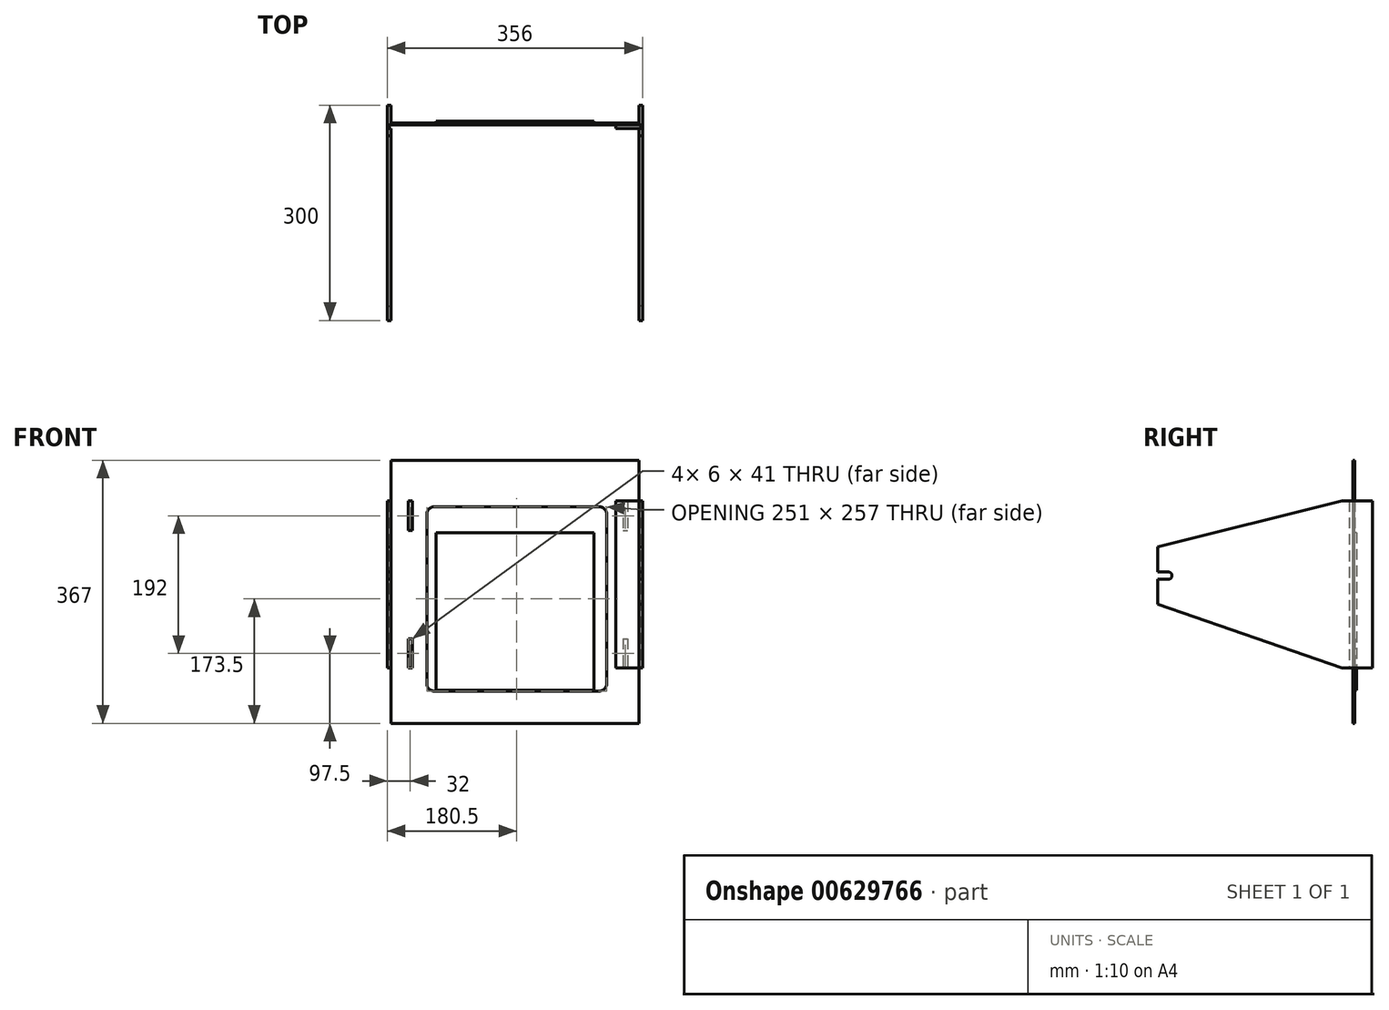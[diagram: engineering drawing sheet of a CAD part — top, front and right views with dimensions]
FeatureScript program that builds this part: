
annotation { "Feature Type Name" : "Feature", "Feature Type Description" : "" }
export const myFeature = defineFeature(function(context is Context, id is Id, definition is map)
    precondition{}
    {
        {
            var Q0;
            Q0=qCreatedBy(makeId("Front.planeOp"),FACE);
            var sketch = newSketch(context, id + "F0", { "sketchPlane" : qUnion([Q0])});
            skLineSegment(sketch, "E0.bottom", {"start": v(118, -138.5) * mm, "end": v(-113, -138.5) * mm});
            skLineSegment(sketch, "E0.top", {"start": v(118, 118.5) * mm, "end": v(-113, 118.5) * mm});
            skLineSegment(sketch, "E0.left", {"start": v(128, -128.5) * mm, "end": v(128, 108.5) * mm});
            skLineSegment(sketch, "E0.right", {"start": v(-123, -128.5) * mm, "end": v(-123, 108.5) * mm});
            skLineSegment(sketch, "E1.bottom", {"start": v(173, -183.5) * mm, "end": v(-173, -183.5) * mm});
            skLineSegment(sketch, "E1.top", {"start": v(173, 183.5) * mm, "end": v(-173, 183.5) * mm});
            skLineSegment(sketch, "E1.left", {"start": v(173, -183.5) * mm, "end": v(173, 183.5) * mm});
            skLineSegment(sketch, "E1.right", {"start": v(-173, -183.5) * mm, "end": v(-173, 183.5) * mm});
            skPoint(sketch, "E1.middle", {"position": v(0, 0) * mm});
            skLineSegment(sketch, "E2.bottom", {"start": v(-110, 82.5) * mm, "end": v(110, 82.5) * mm});
            skLineSegment(sketch, "E2.top", {"start": v(-110, -137.5) * mm, "end": v(110, -137.5) * mm});
            skLineSegment(sketch, "E2.left", {"start": v(-110, 82.5) * mm, "end": v(-110, -137.5) * mm});
            skLineSegment(sketch, "E2.right", {"start": v(110, 82.5) * mm, "end": v(110, -137.5) * mm});
            skLineSegment(sketch, "E3", {"start": v(0, 82.5) * mm, "end": v(0, 183.5) * mm, "construction": true});
            skLineSegment(sketch, "E4.bottom", {"start": v(-149, 126.5) * mm, "end": v(-143, 126.5) * mm});
            skLineSegment(sketch, "E4.top", {"start": v(-149, 85.5) * mm, "end": v(-143, 85.5) * mm});
            skLineSegment(sketch, "E4.left", {"start": v(-149, 126.5) * mm, "end": v(-149, 85.5) * mm});
            skLineSegment(sketch, "E4.right", {"start": v(-143, 126.5) * mm, "end": v(-143, 85.5) * mm});
            skLineSegment(sketch, "E5.bottom", {"start": v(-149, -65.5) * mm, "end": v(-143, -65.5) * mm});
            skLineSegment(sketch, "E5.top", {"start": v(-149, -106.5) * mm, "end": v(-143, -106.5) * mm});
            skLineSegment(sketch, "E5.left", {"start": v(-149, -65.5) * mm, "end": v(-149, -106.5) * mm});
            skLineSegment(sketch, "E5.right", {"start": v(-143, -65.5) * mm, "end": v(-143, -106.5) * mm});
            skLineSegment(sketch, "E6.bottom", {"start": v(151, 126.5) * mm, "end": v(157, 126.5) * mm});
            skLineSegment(sketch, "E6.top", {"start": v(151, 85.5) * mm, "end": v(157, 85.5) * mm});
            skLineSegment(sketch, "E6.left", {"start": v(151, 126.5) * mm, "end": v(151, 85.5) * mm});
            skLineSegment(sketch, "E6.right", {"start": v(157, 126.5) * mm, "end": v(157, 85.5) * mm});
            skLineSegment(sketch, "E7.bottom", {"start": v(151, -65.5) * mm, "end": v(157, -65.5) * mm});
            skLineSegment(sketch, "E7.top", {"start": v(151, -106.5) * mm, "end": v(157, -106.5) * mm});
            skLineSegment(sketch, "E7.left", {"start": v(151, -65.5) * mm, "end": v(151, -106.5) * mm});
            skLineSegment(sketch, "E7.right", {"start": v(157, -65.5) * mm, "end": v(157, -106.5) * mm});
            skPoint(sketch, "E8.visualSharp", {"position": v(-123, 118.5) * mm});
            skArc(sketch, "E8.filletArc", {"start": v(-113, 118.5) * mm, "mid": v(-120.07, 115.57) * mm, "end": v(-123, 108.5) * mm});
            skPoint(sketch, "E9.visualSharp", {"position": v(128, 118.5) * mm});
            skArc(sketch, "E9.filletArc", {"start": v(128, 108.5) * mm, "mid": v(125.07, 115.57) * mm, "end": v(118, 118.5) * mm});
            skPoint(sketch, "E10.visualSharp", {"position": v(128, -138.5) * mm});
            skArc(sketch, "E10.filletArc", {"start": v(118, -138.5) * mm, "mid": v(125.07, -135.57) * mm, "end": v(128, -128.5) * mm});
            skPoint(sketch, "E11.visualSharp", {"position": v(-123, -138.5) * mm});
            skArc(sketch, "E11.filletArc", {"start": v(-123, -128.5) * mm, "mid": v(-120.07, -135.57) * mm, "end": v(-113, -138.5) * mm});
            skLineSegment(sketch, "E12", {"start": v(110, 82.5) * mm, "end": v(-110, -137.5) * mm, "construction": true});
            skLineSegment(sketch, "E13", {"start": v(-110, 82.5) * mm, "end": v(110, -137.5) * mm, "construction": true});
            skSolve(sketch);
        }
        {
            var Q0;
            Q0=makeQuery(id+"F0.imprint","IMPRINT",FACE,{"disambiguationData":[TD([[makeQuery(id+"F0.imprint","IMPRINT",EDGE,{"derivedFrom":sQuery(id+"F0.wireOp",EDGE,"E0.bottom")}),1.0]])]});
            extrude(context, id + "F1", {"entities" : qUnion([Q0]), "oppositeDirection" : true, "depth" : 2.5 * mm, "offsetDistance" : 25 * mm});
        }
        {
            var Q0;
            Q0=makeQuery(id+"F0.imprint","IMPRINT",FACE,{"disambiguationData":[TD([[makeQuery(id+"F0.imprint","IMPRINT",EDGE,{"derivedFrom":sQuery(id+"F0.wireOp",EDGE,"E2.bottom")}),-1.0]])]});
            extrude(context, id + "F2", {"entities" : qUnion([Q0]), "oppositeDirection" : true, "depth" : 5 * mm, "offsetDistance" : 25 * mm});
        }
        {
            var Q0;
            Q0=makeQuery(id+"F1.opExtrude","SWEPT_FACE",FACE,{"disambiguationData":[OSD([sQuery(id+"F0.wireOp",EDGE,"E1.left")])]});
            var sketch = newSketch(context, id + "F3", { "sketchPlane" : qUnion([Q0])});
            skPoint(sketch, "E14.0", {"position": v(0, -27.5) * mm});
            skCircle(sketch, "E15", {"center": v(-272.5, 22.5) * mm, "radius": 100.01 * mm, "construction": true});
            skCircle(sketch, "E16", {"center": v(-272.5, 22.5) * mm, "radius": 28.58 * mm, "construction": true});
            skCircle(sketch, "E17", {"center": v(-272.5, 22.5) * mm, "radius": 15.88 * mm, "construction": true});
            skLineSegment(sketch, "E18", {"start": v(-272.5, -77.5) * mm, "end": v(-272.5, 17.5) * mm, "construction": true});
            skLineSegment(sketch, "E19", {"start": v(-272.5, -27.5) * mm, "end": v(0, -27.5) * mm, "construction": true});
            skLineSegment(sketch, "E20", {"start": v(-15, -106.5) * mm, "end": v(-272.5, -17.5) * mm});
            skLineSegment(sketch, "E21", {"start": v(-272.5, -17.5) * mm, "end": v(-272.5, 17.5) * mm});
            skLineSegment(sketch, "E22", {"start": v(-15, 126.5) * mm, "end": v(-272.5, 62.5) * mm});
            skLineSegment(sketch, "E23.bottom", {"start": v(-272.5, 17.5) * mm, "end": v(-257.5, 17.5) * mm});
            skLineSegment(sketch, "E23.top", {"start": v(-272.5, 27.5) * mm, "end": v(-257.5, 27.5) * mm});
            skArc(sketch, "E24", {"start": v(-257.5, 27.5) * mm, "mid": v(-252.5, 22.5) * mm, "end": v(-257.5, 17.5) * mm});
            skLineSegment(sketch, "E25", {"start": v(-272.5, 22.5) * mm, "end": v(-257.5, 22.5) * mm, "construction": true});
            skLineSegment(sketch, "E26.trimOffspring", {"start": v(-272.5, 27.5) * mm, "end": v(-272.5, 62.5) * mm});
            skLineSegment(sketch, "E27.0", {"start": v(27.5, -183.5) * mm, "end": v(27.5, 183.5) * mm});
            skLineSegment(sketch, "E28", {"start": v(-15, -106.5) * mm, "end": v(27.5, -106.5) * mm});
            skLineSegment(sketch, "E29.0", {"start": v(0, -183.5) * mm, "end": v(0, 183.5) * mm, "construction": true});
            skLineSegment(sketch, "E30", {"start": v(-15, 126.5) * mm, "end": v(27.5, 126.5) * mm});
            skLineSegment(sketch, "E31", {"start": v(-15, -106.5) * mm, "end": v(-15, 126.5) * mm, "construction": true});
            skLineSegment(sketch, "E32.0", {"start": v(2.5, -65.5) * mm, "end": v(2.5, -106.5) * mm, "construction": true});
            skLineSegment(sketch, "E33.0", {"start": v(2.5, 126.5) * mm, "end": v(2.5, 85.5) * mm, "construction": true});
            skLineSegment(sketch, "E34", {"start": v(-257.5, 22.5) * mm, "end": v(27.5, 22.5) * mm, "construction": true});
            skSolve(sketch);
        }
        {
            var Q0;
            Q0 = qSketchRegion(id + "F3", true);
            extrude(context, id + "F4", {"entities" : qUnion([Q0]), "depth" : 5 * mm, "offsetDistance" : 25 * mm});
        }
        {
            var Q0;
            Q0=makeQuery(id+"F4.opExtrude","SWEPT_FACE",FACE,{"disambiguationData":[OSD([sQuery(id+"F3.wireOp",EDGE,"E28")])]});
            var sketch = newSketch(context, id + "F5", { "sketchPlane" : qUnion([Q0])});
            skLineSegment(sketch, "E35.0", {"start": v(173, -2.5) * mm, "end": v(173, 0) * mm});
            skLineSegment(sketch, "E36.bottom", {"start": v(173, 0) * mm, "end": v(175.5, 0) * mm});
            skLineSegment(sketch, "E36.top", {"start": v(173, 5) * mm, "end": v(175.5, 5) * mm});
            skLineSegment(sketch, "E36.left", {"start": v(173, 0) * mm, "end": v(173, 5) * mm});
            skLineSegment(sketch, "E36.right", {"start": v(175.5, 0) * mm, "end": v(175.5, 5) * mm});
            skLineSegment(sketch, "E37", {"start": v(175.5, 5) * mm, "end": v(175.5, 15) * mm, "construction": true});
            skSolve(sketch);
        }
        {
            var Q0;
            Q0 = qSketchRegion(id + "F5", true);
            extrude(context, id + "F6", {"entities" : qUnion([Q0]), "operationType" : NewBodyOperationType.REMOVE, "endBound" : BoundingType.THROUGH_ALL, "oppositeDirection" : true, "depth" : 25 * mm, "offsetDistance" : 25 * mm});
        }
        {
            var Q0;
            Q0=makeQuery(id+"F4.opExtrude","SWEPT_BODY",BODY,{"disambiguationData":[OSD([sQuery(id+"F3.wireOp",EDGE,"E20"),sQuery(id+"F3.wireOp",EDGE,"E21"),sQuery(id+"F3.wireOp",EDGE,"E22"),sQuery(id+"F3.wireOp",EDGE,"E23.bottom"),sQuery(id+"F3.wireOp",EDGE,"E23.top"),sQuery(id+"F3.wireOp",EDGE,"E24"),sQuery(id+"F3.wireOp",EDGE,"E26.trimOffspring"),sQuery(id+"F3.wireOp",EDGE,"E27.0"),sQuery(id+"F3.wireOp",EDGE,"E28"),sQuery(id+"F3.wireOp",EDGE,"E30")])]});
            var Q1;
            Q1=qCreatedBy(makeId("Right.planeOp"),FACE);
            mirror(context, id + "F7", {"entities" : qUnion([Q0]), "mirrorPlane" : qUnion([Q1])});
        }
        {
            var Q0;
            Q0=makeQuery(id+"F6.boolean.opBoolean","COPY",FACE,{"derivedFrom":makeQuery(id+"F6.opExtrude","SWEPT_FACE",FACE,{"disambiguationData":[OSD([sQuery(id+"F5.wireOp",EDGE,"E36.right")])]})});
            extrude(context, id + "F8", {"entities" : qUnion([Q0]), "depth" : 35 * mm, "offsetDistance" : 25 * mm});
        }
    });
